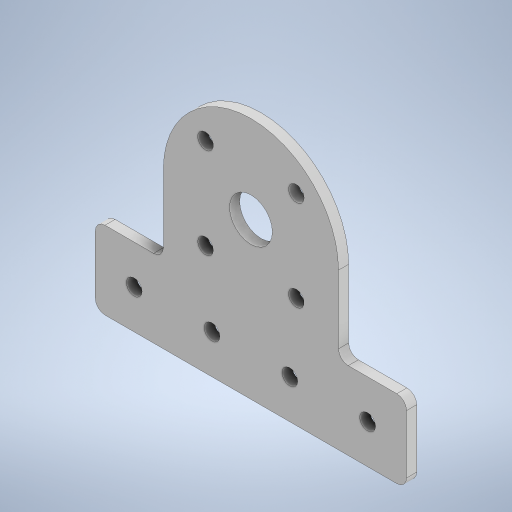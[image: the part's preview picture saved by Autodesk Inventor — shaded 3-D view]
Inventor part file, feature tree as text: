
AUTODESK INVENTOR PART (.ipt)
format: ipt  version: 2024 (Build 280153000, 153)  size: 294,912 bytes
history: native  units: in
note: dims shown in document units (in); Inventor stores cm internally (conversion verified against a paired STEP export)
features: sketch x2, extrude x1, fillet x1, hole x1, pattern_circular x1
ambient origin geometry x8: Origin, YZ Plane, XZ Plane, XY Plane, X Axis, Y Axis, Z Axis, Center Point
bodies: Solid1 (feature_tree)
feature tree (6):
  extrude  "Extrusion1"  Depth=0.13in TaperAngle=0.0deg
  fillet  "Fillet1"  Radius=0.203in
  hole  "Hole1"  [1 undecoded]
  pattern_circular  "Circular Pattern1"  [2 undecoded]
  sketch  "Sketch1"  dims[d1=0.5512in d8=0.13in d9=0.0in d10=0.203in]
  sketch  "Sketch2"  dims[d11=0.203in d12=0.5in d13=0.5in d14=0.5in d15=0.5in d16=2.0in d17=1.0in d18=4.0in d19=2.0in d20=1.0in d21=1.0in d22=0.125in d25=1.125in d26=1.0in d27=0.9449in d28=1.65in d29=45.0deg d30=0.201in d31=0.75in d32=0.385in d33=0.25in d34=0.5635in d35=0.64in d36=0.8108in d37=1.5748in d38=360.0deg]
note: 3 required parameter values undecoded (feature->parameter linkage not recoverable at this tier; creation-order binding heuristic only, values carry confidence <= 0.55)
